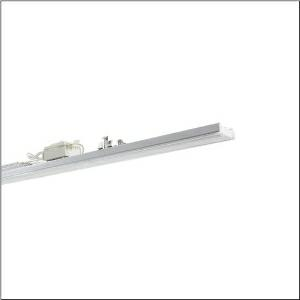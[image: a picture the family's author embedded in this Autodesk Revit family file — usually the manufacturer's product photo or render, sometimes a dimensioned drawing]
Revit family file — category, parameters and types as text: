
# Revit family: licross_r__11_recessed_mo_51tl12dn4axg3s_f752
name_source: partatom
category: Lighting Fixtures
units: mm (PartAtom-declared; Revit-internal decimal feet)

## family parameters
Cut with Voids When Loaded = No
Host = Face
Light Source = No
Part Type = Normal
Room Calculation Point = No
Round Connector Dimension = Use Diameter
Shared = No

## types (1)
- --- (1 x LED, 1010 lm, 6.7 W, 4000K)
    Apparent Load = 7 VA
    CIE Flux Codes = 67 92 99 100 100
    Color Rendering = 80
    Color Temperature = 4000K
    Default Elevation = 1800 mm
    Description = Licross® 11 Recessed MO, luminaire insert, of sheet steel, coil coated, white, length: 1.500mm, width: 66mm, height: 67mm, LED rated luminous flux: 10.240lm, light colour: 840, control gear: DALI 2 (for two DALI lines), with plug, 6-pole, with phase selection, for trunking rail, 14-core, mains connection: 220..240V, AC, 50/60Hz, rated input power: 61W, for trunking rail, 14-core, halogen-free wiring, for emergency light function, converter,control gear: single battery element, battery: LiFePO4, 9Ah, primary optical cover: cover, of PMMA, light emission: direct distribution, primary light characteristic: symmetric, protection rating (complete): IP40, insulation class (complete): insulation class I (protective earthing), certification: CE, UKCA, protection symbol: D if used in an environment without relevant dust loads with corresponding accessories, impact resistance: IK06, permissible ambient temperature for indoor applications: +5..+35°C, standard: EN 60598-2-22, LABS conformity tested according to VDMA 24364:2018-05, reducing of maximum allowable ambient temperature of 5°C with ceiling mounting, corresponds to IFS (International Featured Standards) requirements for safety and quality in the food industry, packaging unit: 1 piece
    Height = 58 mm
    Lamp = 1 x LED
    Lamp Light Flux = 1010 lm
    Lamp Power = 6.7 W
    Lamp count = 1
    Length = 1500 mm
    Luminous efficacy = 151 lm/W
    Manufacturer = Siteco
    ModVariant = No
    Model = 51TL12DN4AXG3S
    Mounting Place = Ceiling
    Mounting Type = Pendant
    Number of Poles = 1
    OnlyDefault = Yes
    Power Factor = 1
    Product Name = Licross® 11 Recessed MO
    Product group = luminaire insert
    ProductGroupID = 902
    Protection Class = Protection class I
    Protection Degree = IP 40
    RLX_Detail_Level = 1
    RLX_Emergency_Light_Flux = 0 lm
    RLX_Emergency_Type = 0
    RLX_Emergency_Type_DB = No
    RlxData = <blob elided: 24741 chars, md5=47acb7e1>
    Socket = socket
    Standby Power = 0 W
    System Light Flux = 1010 lm
    System Power = 7 W
    Type Comments = : emergency light operation: 3 h
    Type Image = l_1296930.jpg
    URL = http://relux.com
    VarID = @adj_090266
    Voltage = 0 V
    Weight = 0.00 kg
    Width = 66 mm

## geometry (parser evidence)
native form markers: Blend x4, Sweep x11
no freeform markers — native parametric forms only
